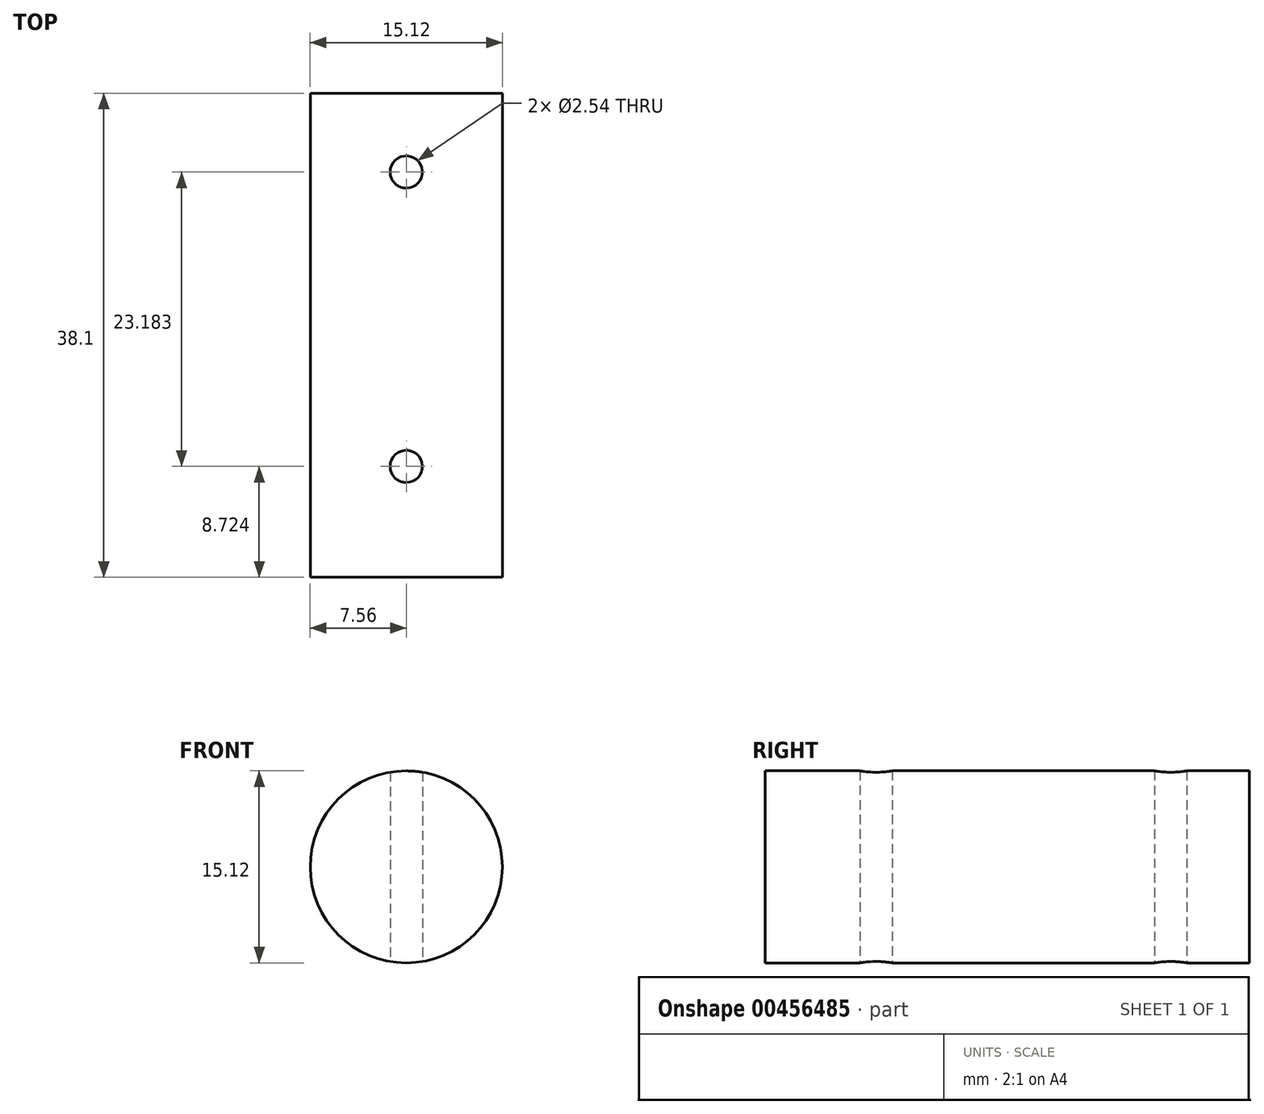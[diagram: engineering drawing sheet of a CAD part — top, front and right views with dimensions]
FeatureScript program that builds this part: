
annotation { "Feature Type Name" : "Feature", "Feature Type Description" : "" }
export const myFeature = defineFeature(function(context is Context, id is Id, definition is map)
    precondition{}
    {
        {
            var Q0;
            Q0=qCreatedBy(makeId("Front.planeOp"),FACE);
            var sketch = newSketch(context, id + "F0", { "sketchPlane" : qUnion([Q0])});
            skCircle(sketch, "E0", {"center": v(0, 0) * mm, "radius": 7.56 * mm});
            skSolve(sketch);
        }
        {
            var Q0;
            Q0 = qSketchRegion(id + "F0", true);
            var Q1;
            Q1=makeQuery(id+"F0.imprint","IMPRINT",FACE,{"disambiguationData":[TD([[makeQuery(id+"F0.imprint","IMPRINT",EDGE,{"derivedFrom":sQuery(id+"F0.wireOp",EDGE,"E0")}),1.0]])]});
            extrude(context, id + "F1", {"entities" : qUnion([Q0, Q1]), "depth" : 38.1 * mm, "offsetDistance" : 25.4 * mm});
        }
        {
            var Q0;
            Q0=qCreatedBy(makeId("Top.planeOp"),FACE);
            var sketch = newSketch(context, id + "F2", { "sketchPlane" : qUnion([Q0])});
            skCircle(sketch, "E1", {"center": v(0, -29.38) * mm, "radius": 1.27 * mm});
            skCircle(sketch, "E2", {"center": v(0, -6.2) * mm, "radius": 1.27 * mm});
            skSolve(sketch);
        }
        {
            var Q0;
            Q0 = qSketchRegion(id + "F2", true);
            var Q1;
            Q1=sQuery(id+"F2.wireOp",EDGE,"E1");
            var Q2;
            Q2=sQuery(id+"F2.wireOp",EDGE,"E2");
            extrude(context, id + "F3", {"entities" : qUnion([Q0]), "operationType" : NewBodyOperationType.REMOVE, "surfaceEntities" : qUnion([Q1, Q2]), "endBound" : BoundingType.SYMMETRIC, "depth" : 25.4 * mm, "offsetDistance" : 25.4 * mm});
        }
    });
